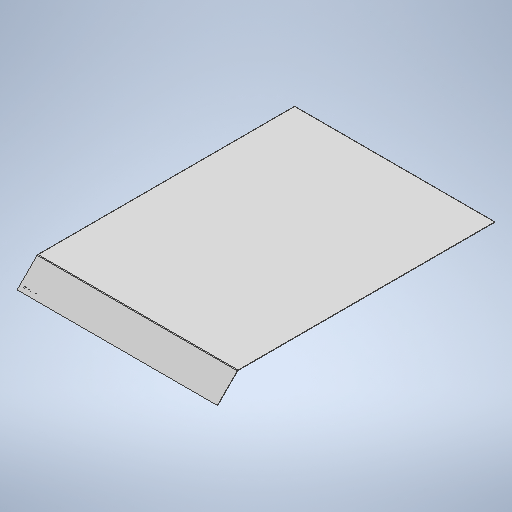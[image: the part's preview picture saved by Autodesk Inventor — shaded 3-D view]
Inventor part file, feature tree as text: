
AUTODESK INVENTOR PART (.ipt)
format: ipt  version: 2025 (Build 290162010, 162A)  size: 325,632 bytes
history: native  units: mm
features: sheet_metal_op x4, other x4, sketch x3
ambient origin geometry x8: Origin, YZ Plane, XZ Plane, XY Plane, X Axis, Y Axis, Z Axis, Center Point
bodies: Solid1 (feature_tree)
feature tree (11):
  sheet_metal_op  "Face1"
  sheet_metal_op  "Flange2"
  other  "Mark1"
  sketch  "Sketch1"  dims[d0=1479.0mm]
  other  "Plate1"
  sketch  "Sketch3"  dims[d1=1900.0mm]
  other  "Plate3"
  sheet_metal_op  "Bend2"
  sheet_metal_op  "Corner2"
  sketch  "Sketch4"  dims[d2=3.0mm d13=3.0mm d14=1.5mm d15=6.0mm d16=5.0mm d17=212.0mm d18=45.0deg d19=5.0mm d20=12.0mm d21=3.0mm d22=5.0mm d23=200.0mm d24=11.661mm d25=25.0mm d26=25.0mm]
  other  "Definition1"
